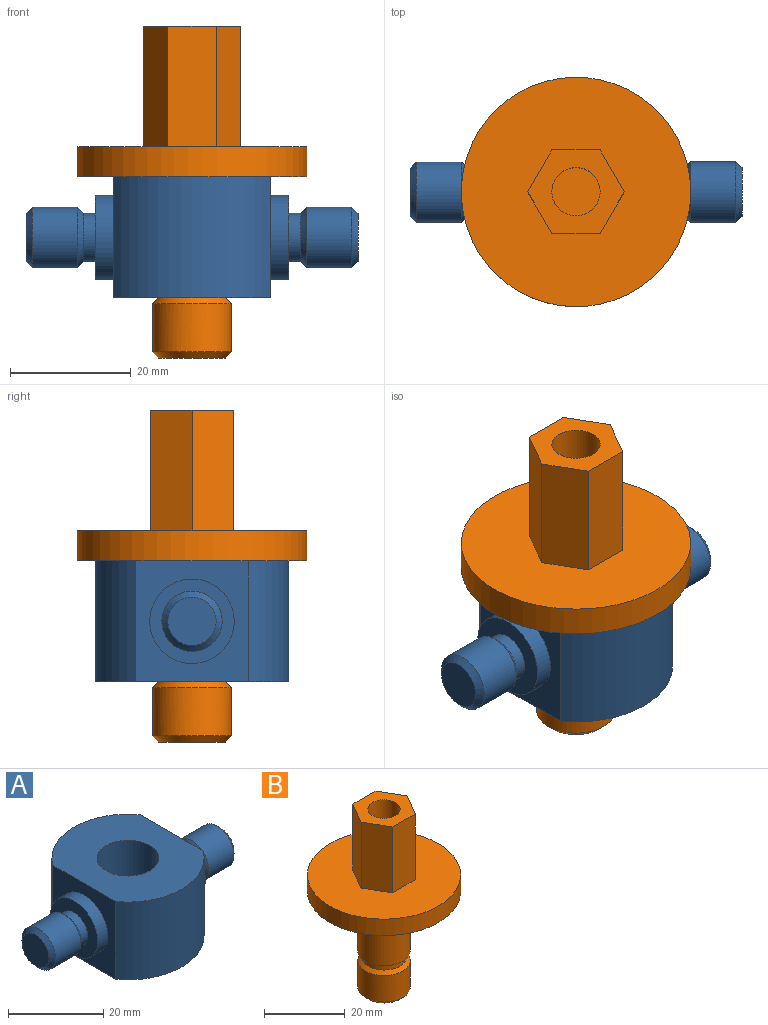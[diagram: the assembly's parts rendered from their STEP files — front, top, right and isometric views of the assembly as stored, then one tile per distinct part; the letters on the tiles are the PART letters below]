
ASSEMBLY  parts=2 mates=1
PART A: 21 faces, bbox 55x32x20 mm
  f0: cylinder r=16mm len=26mm, axis (0,0,1), area 607mm2, adj f2,f3,f5,f6
  f1: cylinder r=16mm len=26mm, axis (0,0,1), area 607mm2, adj f2,f3,f5,f6
  f2: plane 32x26mm, normal (0,0,-1), area 595.4mm2, adj f0,f1,f4,f5,f6
  f3: plane 32x26mm, normal (0,0,1), area 595.4mm2, adj f0,f1,f4,f5,f6
  f4: cylinder r=6.5mm len=20mm, axis (0,0,1), area 816.8mm2, adj f2,f3
  f5: plane 20x18.65mm, normal (1,0,0), area 219.2mm2, adj f0,f1,f2,f3,f9
  f6: plane 20x18.65mm, normal (-1,0,0), area 219.2mm2, adj f0,f1,f2,f3,f7
  f7: cylinder r=7mm len=14mm, axis (1,0,0), area 131.9mm2, adj f6,f8
  f8: plane 14x14mm, normal (-1,0,0), area 103.7mm2, adj f7,f11
  f9: cylinder r=7mm len=14mm, axis (-1,0,0), area 131.9mm2, adj f5,f10
  f10: plane 14x14mm, normal (1,0,0), area 103.7mm2, adj f9,f12
  f11: cylinder r=4mm len=8mm, axis (1,0,0), area 50.3mm2, adj f8,f19
  f12: cylinder r=4mm len=8mm, axis (-1,0,0), area 50.3mm2, adj f10,f17
  f13: cylinder r=5mm len=10mm, axis (1,0,0), area 235.6mm2, adj f19,f20
  f14: plane 8x8mm, normal (-1,0,0), area 50.3mm2, adj f20
  f15: cylinder r=5mm len=10mm, axis (-1,0,0), area 235.6mm2, adj f17,f18
  f16: plane 8x8mm, normal (1,0,0), area 50.3mm2, adj f18
  f17: cone r=5mm half-angle=45deg, axis (1,0,0), area 40mm2, adj f12,f15
  f18: cone r=4mm half-angle=45deg, axis (-1,0,0), area 40mm2, adj f15,f16
  f19: cone r=5mm half-angle=45deg, axis (-1,0,0), area 40mm2, adj f11,f13
  f20: cone r=4mm half-angle=45deg, axis (1,0,0), area 40mm2, adj f13,f14
PART B: 19 faces, bbox 38x38x55 mm
  f0: plane 38x38mm, normal (0,0,1), area 967.8mm2, adj f7,f8,f9,f10,f11,f12,f13
  f1: plane 11x11mm, normal (0,0,-1), area 95mm2, adj f18
  f2: cylinder r=6.5mm len=13mm, axis (0,0,1), area 326.7mm2, adj f17,f18
  f3: cylinder r=5.5mm len=11mm, axis (0,0,1), area 69.1mm2, adj f4,f17
  f4: plane 13x13mm, normal (0,0,-1), area 37.7mm2, adj f3,f5
  f5: cylinder r=6.5mm len=18mm, axis (0,0,1), area 735.1mm2, adj f4,f6
  f6: plane 38x38mm, normal (0,0,-1), area 1001.4mm2, adj f5,f7
  f7: cylinder r=19mm len=38mm, axis (0,0,1), area 596.9mm2, adj f0,f6
  f8: plane 20x6.93mm, normal (0.87,-0.5,0), area 160mm2, adj f0,f9,f13,f14
  f9: plane 20x6.93mm, normal (0.87,0.5,0), area 160mm2, adj f0,f8,f10,f14
  f10: plane 20x8mm, normal (0,1,0), area 160mm2, adj f0,f9,f11,f14
  f11: plane 20x6.93mm, normal (-0.87,0.5,0), area 160mm2, adj f0,f10,f12,f14
  f12: plane 20x6.93mm, normal (-0.87,-0.5,0), area 160mm2, adj f0,f11,f13,f14
  f13: plane 20x8mm, normal (0,-1,0), area 160mm2, adj f0,f8,f12,f14
  f14: plane 16x13.86mm, normal (0,0,1), area 116mm2, adj f8,f9,f10,f11,f12,f13,f15
  f15: cylinder r=4mm len=15mm, axis (0,0,1), area 377mm2, adj f14,f16
  f16: plane 8x8mm, normal (0,0,1), area 50.3mm2, adj f15
  f17: cone r=5.5mm half-angle=45deg, axis (0,0,-1), area 53.3mm2, adj f2,f3
  f18: cone r=6.5mm half-angle=45deg, axis (0,0,1), area 53.3mm2, adj f1,f2
PLACE A t=(0.25,0.76,-19.09)mm fixed
PLACE B t=(0.25,0.76,-19.09)mm
MATE fastened A.f0 <-> B.f15  axis (0,0,1) through (0.25,0.76,10.91)mm
